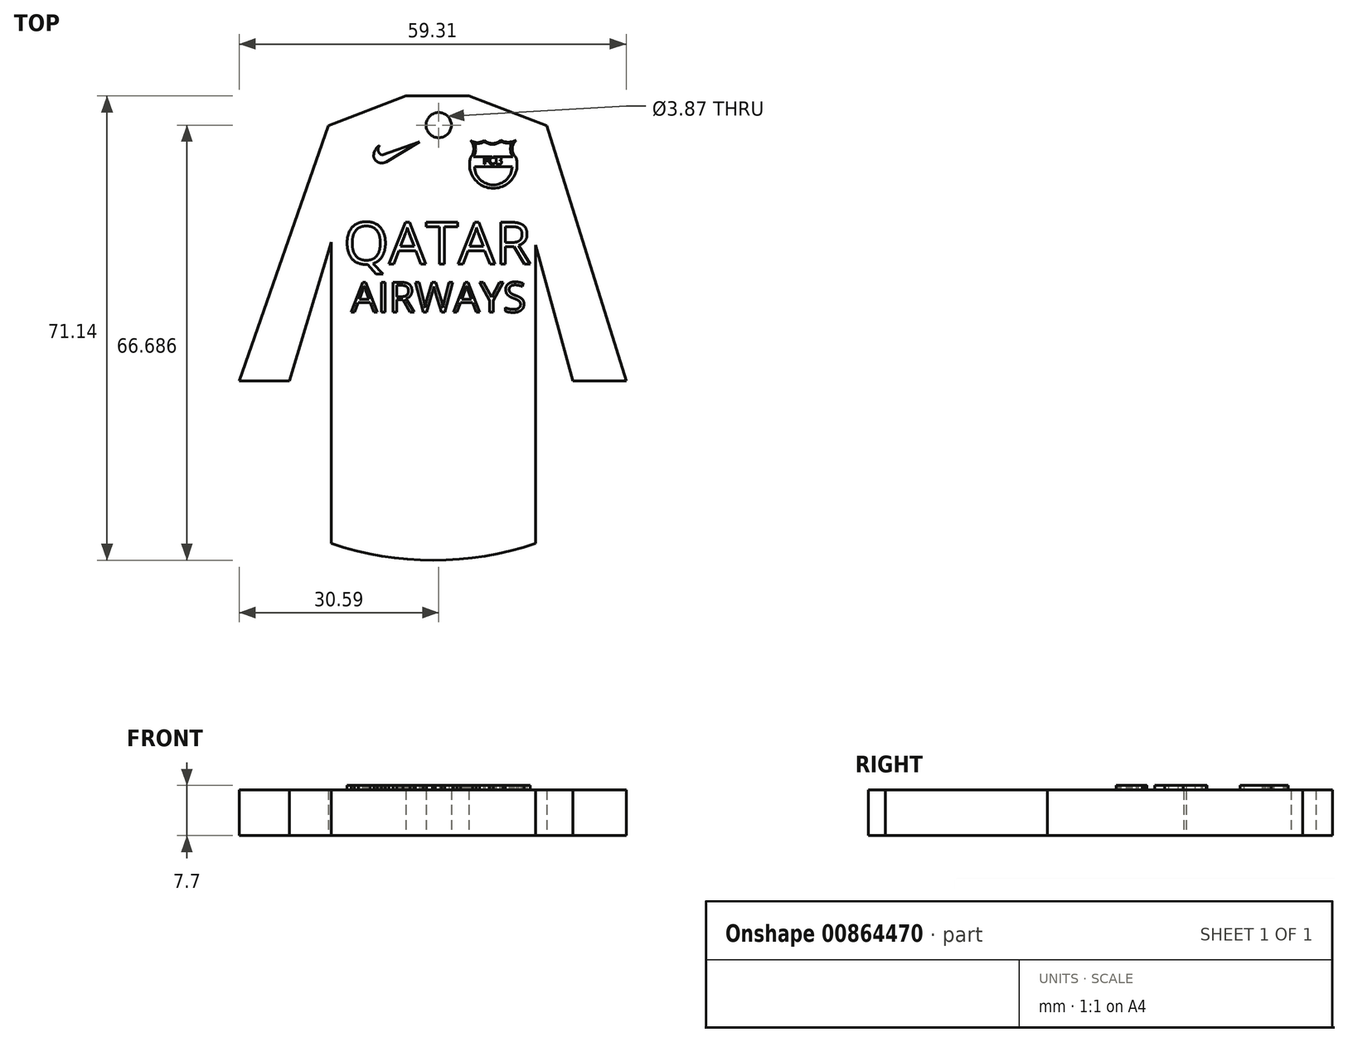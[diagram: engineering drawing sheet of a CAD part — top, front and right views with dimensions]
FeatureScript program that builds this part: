
annotation { "Feature Type Name" : "Feature", "Feature Type Description" : "" }
export const myFeature = defineFeature(function(context is Context, id is Id, definition is map)
    precondition{}
    {
        {
            var Q0;
            Q0=qCreatedBy(makeId("Top.planeOp"),FACE);
            var sketch = newSketch(context, id + "F0", { "sketchPlane" : qUnion([Q0])});
            skPoint(sketch, "E0.end.orphan", {"position": v(-18.93, 37.9) * mm});
            skLineSegment(sketch, "E1.0", {"start": v(-5.04, 42.98) * mm, "end": v(4.63, 42.98) * mm});
            skLineSegment(sketch, "E1.1", {"start": v(-16.49, -25.57) * mm, "end": v(-16.49, 20.58) * mm});
            skLineSegment(sketch, "E1.2", {"start": v(-16.49, 20.58) * mm, "end": v(-22.88, -0.7) * mm});
            skLineSegment(sketch, "E1.3", {"start": v(-22.88, -0.7) * mm, "end": v(-30.59, -0.7) * mm});
            skLineSegment(sketch, "E1.4", {"start": v(-16.92, 38.43) * mm, "end": v(-30.59, -0.7) * mm});
            skArc(sketch, "E1.5", {"start": v(-16.49, -25.57) * mm, "mid": v(-0.83, -28.16) * mm, "end": v(14.82, -25.57) * mm});
            skLineSegment(sketch, "E1.6", {"start": v(-5.04, 42.98) * mm, "end": v(-16.92, 38.43) * mm});
            skLineSegment(sketch, "E1.7", {"start": v(14.82, -25.57) * mm, "end": v(14.82, 20.16) * mm});
            skLineSegment(sketch, "E1.8", {"start": v(14.82, 20.16) * mm, "end": v(20.56, -0.7) * mm});
            skLineSegment(sketch, "E1.9", {"start": v(28.72, -0.7) * mm, "end": v(20.56, -0.7) * mm});
            skLineSegment(sketch, "E1.10", {"start": v(16.57, 38.42) * mm, "end": v(28.72, -0.7) * mm});
            skLineSegment(sketch, "E1.11", {"start": v(4.63, 42.98) * mm, "end": v(16.57, 38.42) * mm});
            skPoint(sketch, "E2.end.orphan", {"position": v(-16.36, 37.9) * mm});
            skPoint(sketch, "E3.start.orphan", {"position": v(16, 37.9) * mm});
            skPoint(sketch, "E4.end.orphan", {"position": v(21.1, 0) * mm});
            skPoint(sketch, "E4.start.orphan", {"position": v(27.77, 0) * mm});
            skPoint(sketch, "E5.end.orphan", {"position": v(14.12, 25.34) * mm});
            skPoint(sketch, "E6.end.orphan", {"position": v(14.12, -25.06) * mm});
            skPoint(sketch, "E7.start.orphan", {"position": v(-15.79, -25.06) * mm});
            skPoint(sketch, "E8.start.orphan", {"position": v(-15.79, 25.34) * mm});
            skPoint(sketch, "E9.start.orphan", {"position": v(-23.4, 0) * mm});
            skSolve(sketch);
        }
        {
            var Q0;
            Q0 = qSketchRegion(id + "F0", true);
            extrude(context, id + "F1", {"entities" : qUnion([Q0]), "depth" : 7 * mm, "offsetDistance" : 25 * mm});
        }
        {
            var Q0;
            Q0=qCreatedBy(makeId("Top.planeOp"),FACE);
            var sketch = newSketch(context, id + "F2", { "sketchPlane" : qUnion([Q0])});
            skArc(sketch, "E10", {"start": v(4.89, 33.56) * mm, "mid": v(5.38, 34.87) * mm, "end": v(4.89, 36.19) * mm});
            skArc(sketch, "E11", {"start": v(4.89, 36.19) * mm, "mid": v(5.94, 35.86) * mm, "end": v(6.99, 36.19) * mm});
            skArc(sketch, "E12", {"start": v(6.99, 36.19) * mm, "mid": v(8.23, 35.73) * mm, "end": v(9.48, 36.19) * mm});
            skArc(sketch, "E13", {"start": v(9.48, 36.19) * mm, "mid": v(10.66, 35.92) * mm, "end": v(11.84, 36.19) * mm});
            skArc(sketch, "E14", {"start": v(11.84, 36.19) * mm, "mid": v(11.28, 34.87) * mm, "end": v(11.84, 33.56) * mm});
            skArc(sketch, "E15", {"start": v(4.89, 33.56) * mm, "mid": v(8.37, 28.84) * mm, "end": v(11.84, 33.56) * mm});
            skLineSegment(sketch, "E16", {"start": v(8.23, 35.73) * mm, "end": v(8.23, 33.7) * mm});
            skLineSegment(sketch, "E17", {"start": v(5.48, 32.18) * mm, "end": v(11.25, 32.18) * mm});
            skArc(sketch, "E18", {"start": v(5.48, 32.18) * mm, "mid": v(8.36, 29.36) * mm, "end": v(11.25, 32.18) * mm});
            skText(sketch, "E19", { "text": "FCB", "fontName": "OpenSans-Regular.ttf"});
            skArc(sketch, "E20.0", {"start": v(5.34, 33.7) * mm, "mid": v(5.67, 34.8) * mm, "end": v(5.4, 35.93) * mm});
            skLineSegment(sketch, "E21", {"start": v(8.23, 33.7) * mm, "end": v(5.34, 33.7) * mm});
            skArc(sketch, "E22.0", {"start": v(11.31, 36) * mm, "mid": v(10.99, 34.84) * mm, "end": v(11.35, 33.7) * mm});
            skLineSegment(sketch, "E23", {"start": v(8.23, 33.7) * mm, "end": v(11.35, 33.7) * mm});
            skArc(sketch, "E24.0", {"start": v(9.5, 36.01) * mm, "mid": v(10.34, 35.78) * mm, "end": v(11.21, 35.82) * mm});
            skArc(sketch, "E24.1", {"start": v(6.98, 36) * mm, "mid": v(8.24, 35.58) * mm, "end": v(9.5, 36.01) * mm});
            skArc(sketch, "E24.2", {"start": v(5.5, 35.76) * mm, "mid": v(6.26, 35.73) * mm, "end": v(6.98, 36) * mm});
            const initialGuessF2  = {"E19": [0.00678, 0.03251, 1, 0, 0.00118]};
            skSetInitialGuess(sketch, initialGuessF2);
            skSolve(sketch);
        }
        {
            var Q0;
            Q0=qCreatedBy(makeId("Top.planeOp"),FACE);
            var sketch = newSketch(context, id + "F3", { "sketchPlane" : qUnion([Q0])});
            skArc(sketch, "E25", {"start": v(-9.96, 33.7) * mm, "mid": v(-9.24, 32.8) * mm, "end": v(-8.1, 32.88) * mm});
            skArc(sketch, "E26", {"start": v(-9.07, 35.4) * mm, "mid": v(-9.76, 34.67) * mm, "end": v(-9.96, 33.7) * mm});
            skArc(sketch, "E27", {"start": v(-9.07, 35.4) * mm, "mid": v(-9.27, 34.59) * mm, "end": v(-8.74, 33.95) * mm});
            skLineSegment(sketch, "E28", {"start": v(-8.74, 33.95) * mm, "end": v(-2.92, 35.93) * mm});
            skLineSegment(sketch, "E29", {"start": v(-2.92, 35.93) * mm, "end": v(-8.1, 32.88) * mm});
            skSolve(sketch);
        }
        {
            var Q0;
            Q0 = qSketchRegion(id + "F3", true);
            extrude(context, id + "F4", {"entities" : qUnion([Q0]), "operationType" : NewBodyOperationType.ADD, "depth" : 7.7 * mm, "offsetDistance" : 25 * mm});
        }
        {
            var Q0;
            Q0=qCreatedBy(makeId("Top.planeOp"),FACE);
            var sketch = newSketch(context, id + "F5", { "sketchPlane" : qUnion([Q0])});
            skText(sketch, "E30", { "text": "QATAR", "fontName": "OpenSans-Regular.ttf"});
            const initialGuessF5  = {"E30": [-0.01458, 0.01725, 1, 0, 0.00643]};
            skSetInitialGuess(sketch, initialGuessF5);
            skSolve(sketch);
        }
        {
            var Q0;
            Q0 = qSketchRegion(id + "F5", true);
            var Q1;
            Q1 = qSketchRegion(id + "F7", true);
            extrude(context, id + "F6", {"entities" : qUnion([Q0, Q1]), "operationType" : NewBodyOperationType.ADD, "depth" : 7.7 * mm, "offsetDistance" : 25 * mm});
        }
        {
            var Q0;
            Q0=qCreatedBy(makeId("Top.planeOp"),FACE);
            var sketch = newSketch(context, id + "F7", { "sketchPlane" : qUnion([Q0])});
            skText(sketch, "E31", { "text": "AIRWAYS", "fontName": "OpenSans-Regular.ttf"});
            const initialGuessF7  = {"E31": [-0.01344, 0.00988, 1, 0, 0.0046]};
            skSetInitialGuess(sketch, initialGuessF7);
            skSolve(sketch);
        }
        {
            var Q0;
            Q0 = qSketchRegion(id + "F7", true);
            extrude(context, id + "F8", {"entities" : qUnion([Q0]), "operationType" : NewBodyOperationType.ADD, "depth" : 7.7 * mm, "offsetDistance" : 25 * mm});
        }
        {
            var Q0;
            Q0=qCreatedBy(makeId("Top.planeOp"),FACE);
            var sketch = newSketch(context, id + "F9", { "sketchPlane" : qUnion([Q0])});
            skCircle(sketch, "E32", {"center": v(0, 38.53) * mm, "radius": 1.93 * mm});
            skSolve(sketch);
        }
        {
            var Q0;
            Q0 = qSketchRegion(id + "F9", true);
            extrude(context, id + "F10", {"entities" : qUnion([Q0]), "operationType" : NewBodyOperationType.REMOVE, "depth" : 26 * mm, "offsetDistance" : 25 * mm});
        }
        {
            var Q0;
            Q0 = qSketchRegion(id + "F3", true);
            extrude(context, id + "F11", {"entities" : qUnion([Q0]), "operationType" : NewBodyOperationType.ADD, "depth" : 7.7 * mm, "offsetDistance" : 25 * mm});
        }
        {
            var Q0;
            Q0 = qSketchRegion(id + "F2", true);
            extrude(context, id + "F12", {"entities" : qUnion([Q0]), "operationType" : NewBodyOperationType.ADD, "depth" : 7.7 * mm, "offsetDistance" : 25 * mm});
        }
        {
            var Q0;
            Q0 = qSketchRegion(id + "F9", true);
            extrude(context, id + "F13", {"entities" : qUnion([Q0]), "operationType" : NewBodyOperationType.REMOVE, "depth" : 11.1 * mm, "offsetDistance" : 25 * mm});
        }
        {
            var Q0;
            Q0 = qSketchRegion(id + "F5", true);
            extrude(context, id + "F14", {"entities" : qUnion([Q0]), "operationType" : NewBodyOperationType.ADD, "depth" : 7.7 * mm, "offsetDistance" : 25 * mm});
        }
        {
            var Q0;
            Q0 = qSketchRegion(id + "F7", true);
            extrude(context, id + "F15", {"entities" : qUnion([Q0]), "operationType" : NewBodyOperationType.ADD, "depth" : 7.7 * mm, "offsetDistance" : 25 * mm});
        }
    });
